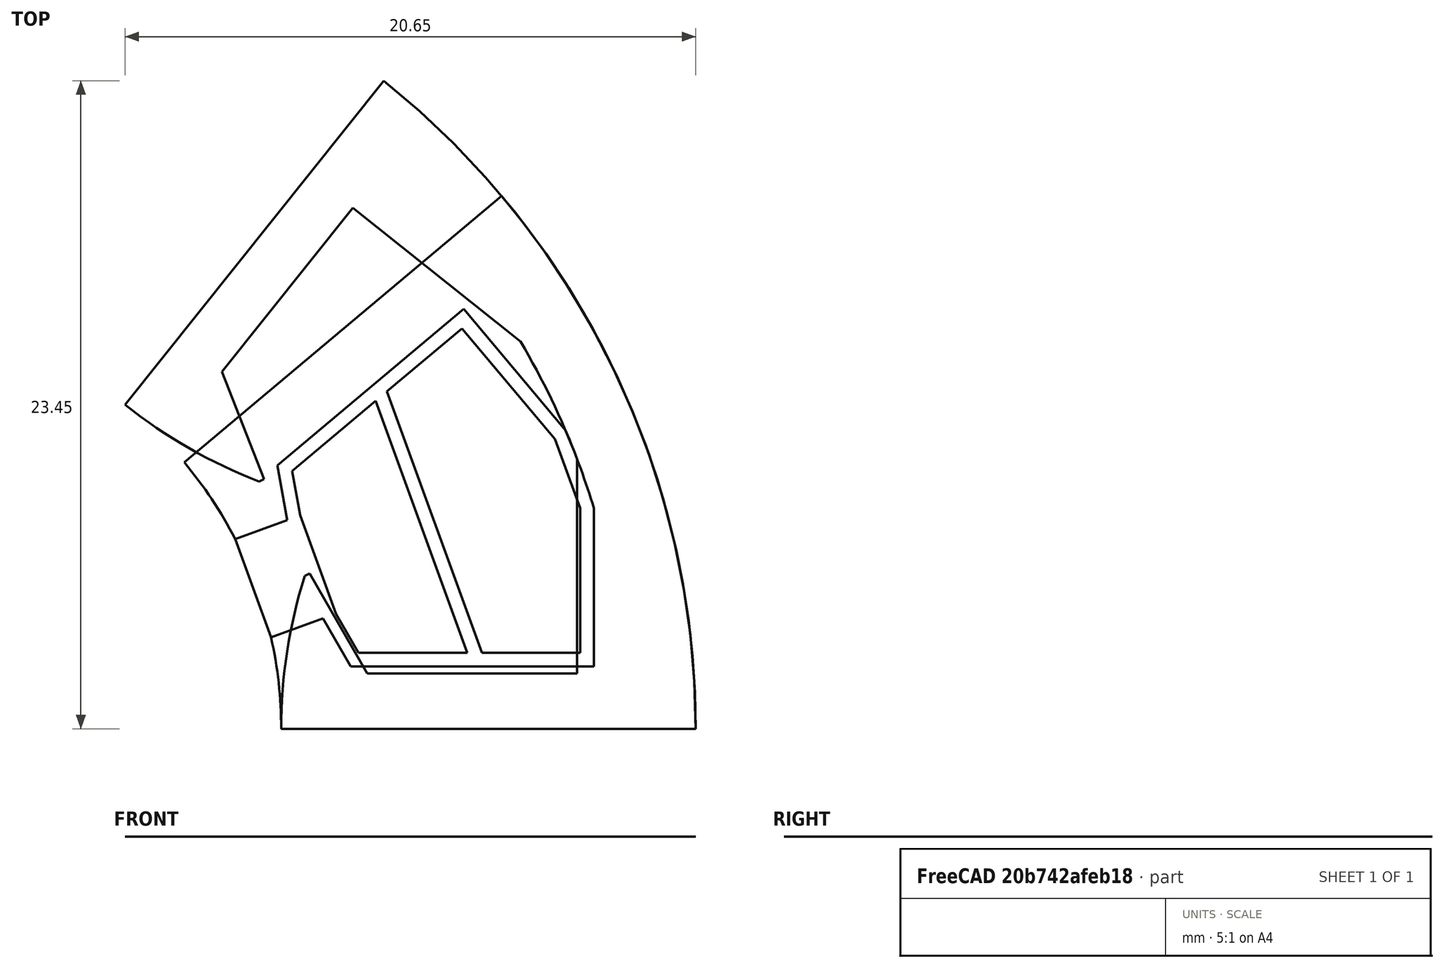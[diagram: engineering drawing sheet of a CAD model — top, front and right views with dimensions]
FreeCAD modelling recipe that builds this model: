
FCSTD DOCUMENT  (FreeCAD 0.18R4 (GitTag))
Label: StatorIRNeedleWindingCoilSpan
License: All rights reserved
LicenseURL: http://en.wikipedia.org/wiki/All_rights_reserved
objects: Sketcher::SketchObject×10, Surface::Filling×5, PartDesign::Body×2, Spreadsheet::Sheet×1
note: 17 computed .brp shape members not serialized (recipe doc carries the construction recipe); baked Part::Feature solids carry a one-line shape summary decoded from their .brp

FEATURE [Spreadsheet::Sheet] Spreadsheet  label="Variables"
  cells = A2=slotNumber; B2(slotNumber)=9; A3=outerDiameter; B3(outerDiameter)=60; A4=innerDiameter; B4(innerDiameter)=30; A5=stackLength; B5(stackLength)=20; A6=stackingFactor; B6(stackingFactor)=0.95; A7=cuttingThickness; B7(cuttingThickness)=0.1; A8=skewAngle; B8(skewAngle)=0; A9=segmentAngle; B9(segmentAngle)==360 / slotNumber; A10=tipHeightReduction; B10(tipHeightReduction)=0; A11=toothThickness; B11(toothThickness)=4.5; A12=yokeThickness; B12(yokeThickness)=2.5; A13=tipHeight; B13(tipHeight)=2; A14=tipAngle; B14(tipAngle)=120; A15=openingLeft; B15(openingLeft)=1.9; A16=openingRight; B16(openingRight)=1.9; A17=slotIsolation; B17(slotIsolation)=0.5; A18=windingAngle; B18(windingAngle)=35; A19=heightRatio; B19(heightRatio)=45; A20=roundingRadii; B20(roundingRadii)=0.2; A21=backWidth; B21(backWidth)=3; A22=backAngle; B22(backAngle)=90; A23=phaseSeparation; B23(phaseSeparation)=2; A24=axialOverhang; B24(axialOverhang)=1.2; A25=axialHeight; B25(axialHeight)=3
FEATURE [Sketcher::SketchObject] Sketch003  label="StatorSketch1"
  MapMode = 5
  Support = -> [XY_Plane]
  expr: Constraints[76] = Variables.backWidth
  expr: Constraints[37] = Variables.tipAngle
  expr: Constraints[60] = Variables.backAngle
  expr: Constraints[30] = Variables.tipHeight
  expr: Constraints[28] = Variables.openingRight
  expr: Constraints[32] = Variables.tipHeight * (1 - Variables.tipHeightReduction / 100)
  expr: Constraints[22] = Variables.openingLeft
  expr: Constraints[6] = Variables.outerDiameter / 2
  expr: Constraints[59] = Variables.tipHeight
  expr: Constraints[5] = Variables.segmentAngle
  expr: Constraints[11] = Variables.innerDiameter / 2
  expr: Constraints[54] = Variables.outerDiameter / 2 - Variables.yokeThickness
  expr: Constraints[49] = Variables.tipHeight * (1 - Variables.tipHeightReduction / 100)
  expr: Constraints[58] = Variables.toothThickness / 2
  expr: Constraints[18] = Variables.segmentAngle / 2
  expr: Constraints[50] = Variables.tipAngle
  expr: Constraints[52] = Variables.backAngle
  expr: Constraints[42] = Variables.toothThickness / 2
  sketch-geometry (27):
    g0: LineSegment [constr] StartX=0 StartY=0 StartZ=0 EndX=22.9813 EndY=19.2836 EndZ=0
    g1: LineSegment [constr] StartX=0 StartY=0 StartZ=0 EndX=30 EndY=0 EndZ=0
    g2: ArcOfCircle CenterX=0 CenterY=0 CenterZ=0 NormalX=0 NormalY=0 NormalZ=1 AngleXU=0 Radius=30 StartAngle=0 EndAngle=0.698132
    g3: ArcOfCircle [constr] CenterX=0 CenterY=0 CenterZ=0 NormalX=0 NormalY=0 NormalZ=1 AngleXU=0 Radius=15 StartAngle=0 EndAngle=0.698132
    g4: LineSegment [constr] StartX=13.3338 StartY=6.87098 StartZ=0 EndX=27.4859 EndY=12.0219 EndZ=0
    g5: LineSegment [constr] StartX=14.6308 StartY=3.30731 StartZ=0 EndX=28.7829 EndY=8.45826 EndZ=0
    g6: LineSegment [constr] StartX=28.1908 StartY=10.2606 StartZ=0 EndX=14.0954 EndY=5.1303 EndZ=0
    g7: LineSegment [constr] StartX=0 StartY=0 StartZ=0 EndX=14.0954 EndY=5.1303 EndZ=0
    g8: LineSegment [constr] StartX=13.3338 StartY=6.87098 StartZ=0 EndX=14.0954 EndY=5.1303 EndZ=0
    g9: LineSegment [constr] StartX=14.0954 StartY=5.1303 StartZ=0 EndX=14.6308 EndY=3.30731 EndZ=0
    g10: LineSegment [constr] StartX=13.3338 StartY=6.87098 StartZ=0 EndX=15.2132 EndY=7.55502 EndZ=0
    g11: LineSegment StartX=13.3338 StartY=6.87098 StartZ=0 EndX=15.2132 EndY=7.55502 EndZ=0
    g12: LineSegment StartX=15.2132 StartY=7.55502 StartZ=0 EndX=14.864 EndY=9.53521 EndZ=0
    g13: LineSegment StartX=14.864 StartY=9.53521 StartZ=0 EndX=21.6056 EndY=15.1921 EndZ=0
    g14: LineSegment [constr] StartX=14.864 StartY=9.53521 StartZ=0 EndX=13.4177 EndY=11.2588 EndZ=0
    g15: LineSegment StartX=21.6056 StartY=15.1921 StartZ=0 EndX=25.29 EndY=10.8011 EndZ=0
    g16: LineSegment StartX=26.3161 StartY=7.98201 StartZ=0 EndX=26.3161 EndY=2.25 EndZ=0
    g17: LineSegment StartX=26.3161 StartY=2.25 StartZ=0 EndX=17.5156 EndY=2.25 EndZ=0
    g18: LineSegment StartX=17.5156 StartY=2.25 StartZ=0 EndX=16.5102 EndY=3.99135 EndZ=0
    g19: LineSegment StartX=16.5102 StartY=3.99135 StartZ=0 EndX=14.6308 EndY=3.30731 EndZ=0
    g20: LineSegment [constr] StartX=26.3161 StartY=2.25 StartZ=0 EndX=26.3161 EndY=0 EndZ=0
    g21: LineSegment StartX=11.4907 StartY=9.64181 StartZ=0 EndX=22.9813 EndY=19.2836 EndZ=0
    g22: LineSegment StartX=30 StartY=0 StartZ=0 EndX=15 EndY=0 EndZ=0
    g23: ArcOfCircle CenterX=-3.78e-14 CenterY=0 CenterZ=0 NormalX=0 NormalY=0 NormalZ=1 AngleXU=0 Radius=15 StartAngle=0 EndAngle=0.222314
    g24: ArcOfCircle CenterX=-1.53e-14 CenterY=-1.29e-14 CenterZ=0 NormalX=0 NormalY=0 NormalZ=1 AngleXU=0 Radius=15 StartAngle=0.475817 EndAngle=0.698132
    g25: ArcOfCircle CenterX=0 CenterY=0 CenterZ=0 NormalX=0 NormalY=0 NormalZ=1 AngleXU=0 Radius=27.5 StartAngle=0.294493 EndAngle=0.403638
    g26: LineSegment [constr] StartX=25.29 StartY=10.8011 StartZ=0 EndX=26.3161 EndY=7.98201 EndZ=0
  constraints (77):
    c: Angle(g-1,g1) = 0
    c: Coincident(g0,g-1)
    c: Coincident(g1,g-1)
    c: Coincident(g2,g-1)
    c: Coincident(g2,g0)
    c: Angle(g1,g0) = 0.698132
    c: Radius(g2) = 30
    c: Coincident(g2,g1)
    c: Coincident(g3,g-1)
    c: PointOnObject(g3,g1)
    c: PointOnObject(g3,g0)
    c: Radius(g3) = 15
    c: PointOnObject(g4,g3)
    c: PointOnObject(g4,g2)
    c: PointOnObject(g5,g3)
    c: PointOnObject(g5,g2)
    c: PointOnObject(g6,g2)
    c: PointOnObject(g6,g3)
    c: Angle(g1,g6) = 0.349066
    c: Coincident(g7,g-1)
    c: Coincident(g7,g6)
    c: Coincident(g8,g4)
    c: Distance(g8) = 1.9
    c: Coincident(g8,g6)
    c: Parallel(g4,g6)
    c: Parallel(g5,g6)
    c: Coincident(g9,g6)
    c: Coincident(g9,g5)
    c: Distance(g9) = 1.9
    c: PointOnObject(g10,g4)
    c: Distance(g4,g10) = 2
    c: Angle(g4,g10) = 3.14159
    c: Distance(g10,g10) = 2
    c: Coincident(g11,g10)
    c: Coincident(g12,g11)
    c: Coincident(g13,g12)
    c: Coincident(g11,g10)
    c: Angle(g12,g13) = 2.0944
    c: Parallel(g0,g13)
    c: Coincident(g14,g12)
    c: PointOnObject(g14,g0)
    c: Angle(g13,g14) = 1.5708
    c: Distance(g14) = 2.25
    c: Coincident(g15,g13)
    c: Coincident(g17,g16)
    c: Coincident(g18,g17)
    c: PointOnObject(g18,g5)
    c: Coincident(g19,g18)
    c: PointOnObject(g19,g5)
    c: Distance(g19) = 2
    c: Angle(g17,g18) = 2.0944
    c: Parallel(g17,g1)
    c: Angle(g16,g17) = 1.5708
    c: Symmetric(g15,g16,g6)
    c: Distance(g-1,g15) = 27.5
    c: Coincident(g20,g16)
    c: PointOnObject(g20,g1)
    c: Vertical(g20)
    c: DistanceY(g20,g20) = 2.25
    c: Distance(g5,g18) = 2
    c: Angle(g13,g15) = 1.5708
    c: Coincident(g21,g3)
    c: Coincident(g21,g0)
    c: Coincident(g22,g2)
    c: Coincident(g22,g3)
    c: PointOnObject(g23,g-1)
    c: Coincident(g23,g19)
    c: Coincident(g23,g22)
    c: PointOnObject(g24,g0)
    c: Coincident(g24,g11)
    c: Coincident(g24,g21)
    c: Coincident(g25,g2)
    c: Coincident(g25,g15)
    c: Coincident(g25,g16)
    c: Coincident(g26,g15)
    c: Coincident(g26,g16)
    c: Distance(g26) = 3
FEATURE [Sketcher::SketchObject] Sketch  label="StatorStack"
  MapMode = 5
  Support = -> [XY_Plane001]
  expr: Constraints[20] = Variables.innerDiameter / 2
  expr: Constraints[10] = Variables.outerDiameter / 2
  expr: Constraints[9] = Variables.innerDiameter / 2
  expr: Constraints[8] = Variables.stackLength
  sketch-geometry (8):
    g0: LineSegment StartX=-10 StartY=15 StartZ=0 EndX=10 EndY=15 EndZ=0
    g1: LineSegment StartX=10 StartY=15 StartZ=0 EndX=10 EndY=30 EndZ=0
    g2: LineSegment StartX=10 StartY=30 StartZ=0 EndX=-10 EndY=30 EndZ=0
    g3: LineSegment StartX=-10 StartY=30 StartZ=0 EndX=-10 EndY=15 EndZ=0
    g4: LineSegment StartX=-10 StartY=-15 StartZ=0 EndX=10 EndY=-15 EndZ=0
    g5: LineSegment StartX=10 StartY=-15 StartZ=0 EndX=10 EndY=-30 EndZ=0
    g6: LineSegment StartX=10 StartY=-30 StartZ=0 EndX=-10 EndY=-30 EndZ=0
    g7: LineSegment StartX=-10 StartY=-30 StartZ=0 EndX=-10 EndY=-15 EndZ=0
  constraints (22):
    c: Coincident(g0,g1)
    c: Coincident(g1,g2)
    c: Coincident(g2,g3)
    c: Coincident(g3,g0)
    c: Horizontal(g2)
    c: Vertical(g1)
    c: Vertical(g3)
    c: Symmetric(g0,g0,g-2)
    c: DistanceX(g0,g0) = 20
    c: DistanceY(g-1,g0) = 15
    c: DistanceY(g-1,g1) = 30
    c: Coincident(g4,g5)
    c: Coincident(g5,g6)
    c: Coincident(g6,g7)
    c: Coincident(g7,g4)
    c: Horizontal(g6)
    c: Vertical(g5)
    c: Vertical(g7)
    c: Equal(g4,g0)
    c: Symmetric(g4,g4,g-2)
    c: DistanceY(g4,g-1) = 15
    c: Equal(g7,g3)
FEATURE [Sketcher::SketchObject] Sketch005  label="StatorSketch2"
  MapMode = 5
  Support = -> [XY_Plane]
  expr: Constraints[76] = Variables.backWidth
  expr: Constraints[28] = Variables.openingRight
  expr: Constraints[30] = Variables.tipHeight
  expr: Constraints[51] = Variables.tipAngle
  expr: Constraints[37] = Variables.tipAngle
  expr: Constraints[60] = Variables.tipHeight
  expr: Constraints[32] = Variables.tipHeight * (1 - Variables.tipHeightReduction / 100)
  expr: Constraints[61] = Variables.backAngle
  expr: Constraints[6] = Variables.outerDiameter / 2
  expr: Constraints[5] = Variables.segmentAngle
  expr: Constraints[22] = Variables.openingLeft
  expr: Constraints[55] = Variables.outerDiameter / 2 - Variables.yokeThickness
  expr: Constraints[59] = Variables.toothThickness / 2
  expr: Constraints[50] = Variables.tipHeight * (1 - Variables.tipHeightReduction / 100)
  expr: Constraints[18] = Variables.segmentAngle / 2
  expr: Constraints[11] = Variables.innerDiameter / 2
  expr: Constraints[53] = Variables.backAngle
  expr: Constraints[42] = Variables.toothThickness / 2
  sketch-geometry (27):
    g0: LineSegment [constr] StartX=0 StartY=0 StartZ=0 EndX=18.7047 EndY=23.4549 EndZ=0
    g1: LineSegment [constr] StartX=0 StartY=0 StartZ=0 EndX=30 EndY=0 EndZ=0
    g2: ArcOfCircle CenterX=0 CenterY=0 CenterZ=0 NormalX=0 NormalY=0 NormalZ=1 AngleXU=0 Radius=30 StartAngle=0 EndAngle=0.897598
    g3: ArcOfCircle [constr] CenterX=0 CenterY=0 CenterZ=0 NormalX=0 NormalY=0 NormalZ=1 AngleXU=0 Radius=15 StartAngle=0 EndAngle=0.897598
    g4: LineSegment [constr] StartX=12.5834 StartY=8.16445 StartZ=0 EndX=26.1523 EndY=14.6989 EndZ=0
    g5: LineSegment [constr] StartX=14.2288 StartY=4.74764 StartZ=0 EndX=27.7977 EndY=11.2821 EndZ=0
    g6: LineSegment [constr] StartX=27.0291 StartY=13.0165 StartZ=0 EndX=13.5145 EndY=6.50826 EndZ=0
    g7: LineSegment [constr] StartX=0 StartY=0 StartZ=0 EndX=13.5145 EndY=6.50826 EndZ=0
    g8: LineSegment [constr] StartX=12.5834 StartY=8.16445 StartZ=0 EndX=13.5145 EndY=6.50826 EndZ=0
    g9: LineSegment [constr] StartX=13.5145 StartY=6.50826 StartZ=0 EndX=14.2288 EndY=4.74764 EndZ=0
    g10: LineSegment [constr] StartX=14.2051 StartY=8.94544 StartZ=0 EndX=14.3853 EndY=9.03222 EndZ=0
    g11: LineSegment StartX=14.2051 StartY=8.94544 StartZ=0 EndX=14.3853 EndY=9.03222 EndZ=0
    g12: LineSegment StartX=14.3853 StartY=9.03222 StartZ=0 EndX=12.8601 EndY=12.9183 EndZ=0
    g13: LineSegment StartX=12.8601 StartY=12.9183 StartZ=0 EndX=17.5931 EndY=18.8533 EndZ=0
    g14: LineSegment [constr] StartX=12.8601 StartY=12.9183 StartZ=0 EndX=11.2965 EndY=14.1653 EndZ=0
    g15: LineSegment StartX=17.5931 StartY=18.8533 StartZ=0 EndX=23.6613 EndY=14.0141 EndZ=0
    g16: LineSegment [constr] StartX=23.6613 StartY=14.0141 StartZ=0 EndX=25.7092 EndY=9.7615 EndZ=0
    g17: LineSegment StartX=25.7092 StartY=9.7615 StartZ=0 EndX=25.7092 EndY=2 EndZ=0
    g18: LineSegment StartX=25.7092 StartY=2 StartZ=0 EndX=18.1181 EndY=2 EndZ=0
    g19: LineSegment StartX=18.1181 StartY=2 StartZ=0 EndX=16.0308 EndY=5.61541 EndZ=0
    g20: LineSegment StartX=16.0308 StartY=5.61541 StartZ=0 EndX=15.8506 EndY=5.52863 EndZ=0
    g21: LineSegment [constr] StartX=25.7092 StartY=2 StartZ=0 EndX=25.7092 EndY=0 EndZ=0
    g22: LineSegment StartX=9.35235 StartY=11.7275 StartZ=0 EndX=18.7047 EndY=23.4549 EndZ=0
    g23: LineSegment StartX=30 StartY=0 StartZ=0 EndX=15 EndY=0 EndZ=0
    g24: ArcOfCircle CenterX=20.8201 CenterY=26.1075 CenterZ=0 NormalX=0 NormalY=0 NormalZ=1 AngleXU=0 Radius=18.3928 StartAngle=4.03919 EndAngle=4.3445
    g25: ArcOfCircle CenterX=33.3928 CenterY=0 CenterZ=0 NormalX=0 NormalY=0 NormalZ=1 AngleXU=0 Radius=18.3928 StartAngle=2.83628 EndAngle=3.14159
    g26: ArcOfCircle CenterX=0 CenterY=0 CenterZ=0 NormalX=0 NormalY=0 NormalZ=1 AngleXU=0 Radius=27.5 StartAngle=0.362875 EndAngle=0.534723
  constraints (77):
    c: Angle(g-1,g1) = 0
    c: Coincident(g0,g-1)
    c: Coincident(g1,g-1)
    c: Coincident(g2,g-1)
    c: Coincident(g2,g0)
    c: Angle(g1,g0) = 0.698132
    c: Radius(g2) = 30
    c: Coincident(g2,g1)
    c: Coincident(g3,g-1)
    c: PointOnObject(g3,g1)
    c: PointOnObject(g3,g0)
    c: Radius(g3) = 15
    c: PointOnObject(g4,g3)
    c: PointOnObject(g4,g2)
    c: PointOnObject(g5,g3)
    c: PointOnObject(g5,g2)
    c: PointOnObject(g6,g2)
    c: PointOnObject(g6,g3)
    c: Angle(g1,g6) = 0.349066
    c: Coincident(g7,g-1)
    c: Coincident(g7,g6)
    c: Coincident(g8,g4)
    c: Distance(g8) = 1.9
    c: Coincident(g8,g6)
    c: Parallel(g4,g6)
    c: Parallel(g5,g6)
    c: Coincident(g9,g6)
    c: Coincident(g9,g5)
    c: Distance(g9) = 1.9
    c: PointOnObject(g10,g4)
    c: Distance(g4,g10) = 2
    c: Angle(g4,g10) = 3.14159
    c: Distance(g10,g10) = 2
    c: Coincident(g11,g10)
    c: Coincident(g12,g11)
    c: Coincident(g13,g12)
    c: Coincident(g11,g10)
    c: Angle(g12,g13) = 2.0944
    c: Parallel(g0,g13)
    c: Coincident(g14,g12)
    c: PointOnObject(g14,g0)
    c: Angle(g13,g14) = 1.5708
    c: Distance(g14) = 2.25
    c: Coincident(g15,g13)
    c: Coincident(g16,g15)
    c: Coincident(g17,g16)
    c: Coincident(g18,g17)
    c: Coincident(g19,g18)
    c: PointOnObject(g19,g5)
    c: Coincident(g20,g19)
    c: Distance(g20) = 2
    c: Angle(g18,g19) = 2.0944
    c: Parallel(g18,g1)
    c: Angle(g17,g18) = 1.5708
    c: Symmetric(g15,g16,g6)
    c: Distance(g-1,g15) = 27.5
    c: Coincident(g21,g17)
    c: PointOnObject(g21,g1)
    c: Vertical(g21)
    c: DistanceY(g21,g21) = 2.25
    c: Distance(g5,g19) = 2
    c: Angle(g13,g15) = 1.5708
    c: Coincident(g22,g3)
    c: Coincident(g22,g0)
    c: Coincident(g23,g2)
    c: Coincident(g23,g3)
    c: PointOnObject(g24,g22)
    c: Coincident(g24,g11)
    c: Coincident(g24,g22)
    c: Angle(g5,g20) = 3.14159
    c: PointOnObject(g25,g-1)
    c: Coincident(g25,g20)
    c: Coincident(g25,g23)
    c: Coincident(g26,g2)
    c: Coincident(g26,g15)
    c: Coincident(g26,g17)
    c: Distance(g16) = 3
FEATURE [Sketcher::SketchObject] Sketch008  label="SlotSketch"
  MapMode = 5
  Support = -> [XY_Plane]
  expr: Constraints[50] = Variables.toothThickness / 2
  expr: Constraints[18] = Variables.segmentAngle / 2
  expr: Constraints[30] = Variables.tipAngle
  expr: Constraints[51] = Variables.tipHeight
  expr: Constraints[28] = Variables.openingRight
  expr: Constraints[67] = Variables.backWidth
  expr: Constraints[46] = Variables.outerDiameter / 2 - Variables.yokeThickness
  expr: Constraints[22] = Variables.openingLeft
  expr: Constraints[6] = Variables.outerDiameter / 2
  expr: Constraints[44] = Variables.backAngle
  expr: Constraints[52] = Variables.backAngle
  expr: Constraints[11] = Variables.innerDiameter / 2
  expr: Constraints[5] = Variables.segmentAngle
  expr: Constraints[42] = Variables.tipAngle
  expr: Constraints[35] = Variables.toothThickness / 2
  sketch-geometry (25):
    g0: LineSegment [constr] StartX=0 StartY=0 StartZ=0 EndX=22.9813 EndY=19.2836 EndZ=0
    g1: LineSegment [constr] StartX=0 StartY=0 StartZ=0 EndX=30 EndY=0 EndZ=0
    g2: ArcOfCircle [constr] CenterX=0 CenterY=0 CenterZ=0 NormalX=0 NormalY=0 NormalZ=1 AngleXU=0 Radius=30 StartAngle=0 EndAngle=0.698132
    g3: ArcOfCircle [constr] CenterX=0 CenterY=0 CenterZ=0 NormalX=0 NormalY=0 NormalZ=1 AngleXU=0 Radius=15 StartAngle=0 EndAngle=0.698132
    g4: LineSegment [constr] StartX=13.3338 StartY=6.87098 StartZ=0 EndX=27.4859 EndY=12.0219 EndZ=0
    g5: LineSegment [constr] StartX=14.6308 StartY=3.30731 StartZ=0 EndX=28.7829 EndY=8.45826 EndZ=0
    g6: LineSegment [constr] StartX=28.1908 StartY=10.2606 StartZ=0 EndX=14.0954 EndY=5.1303 EndZ=0
    g7: LineSegment [constr] StartX=0 StartY=0 StartZ=0 EndX=14.0954 EndY=5.1303 EndZ=0
    g8: LineSegment [constr] StartX=13.3338 StartY=6.87098 StartZ=0 EndX=14.0954 EndY=5.1303 EndZ=0
    g9: LineSegment [constr] StartX=14.0954 StartY=5.1303 StartZ=0 EndX=14.6308 EndY=3.30731 EndZ=0
    g10: LineSegment StartX=15.2132 StartY=7.55502 StartZ=0 EndX=14.864 EndY=9.53521 EndZ=0
    g11: LineSegment StartX=14.864 StartY=9.53521 StartZ=0 EndX=21.6056 EndY=15.1921 EndZ=0
    g12: LineSegment [constr] StartX=14.864 StartY=9.53521 StartZ=0 EndX=13.4177 EndY=11.2588 EndZ=0
    g13: LineSegment StartX=21.6056 StartY=15.1921 StartZ=0 EndX=25.29 EndY=10.8011 EndZ=0
    g14: LineSegment [constr] StartX=25.29 StartY=10.8011 StartZ=0 EndX=26.3161 EndY=7.98201 EndZ=0
    g15: LineSegment StartX=26.3161 StartY=7.98201 StartZ=0 EndX=26.3161 EndY=2.25 EndZ=0
    g16: LineSegment StartX=26.3161 StartY=2.25 StartZ=0 EndX=17.5156 EndY=2.25 EndZ=0
    g17: LineSegment StartX=17.5156 StartY=2.25 StartZ=0 EndX=16.5102 EndY=3.99135 EndZ=0
    g18: LineSegment [constr] StartX=26.3161 StartY=2.25 StartZ=0 EndX=26.3161 EndY=0 EndZ=0
    g19: LineSegment [constr] StartX=11.4907 StartY=9.64181 StartZ=0 EndX=22.9813 EndY=19.2836 EndZ=0
    g20: LineSegment [constr] StartX=30 StartY=0 StartZ=0 EndX=15 EndY=0 EndZ=0
    g21: LineSegment StartX=13.3338 StartY=6.87098 StartZ=0 EndX=14.6308 EndY=3.30731 EndZ=0
    g22: LineSegment StartX=13.3338 StartY=6.87098 StartZ=0 EndX=15.2132 EndY=7.55502 EndZ=0
    g23: LineSegment StartX=14.6308 StartY=3.30731 StartZ=0 EndX=16.5102 EndY=3.99135 EndZ=0
    g24: ArcOfCircle CenterX=0 CenterY=0 CenterZ=0 NormalX=0 NormalY=0 NormalZ=1 AngleXU=0 Radius=27.5 StartAngle=0.294493 EndAngle=0.403638
  constraints (68):
    c: Angle(g-1,g1) = 0
    c: Coincident(g0,g-1)
    c: Coincident(g1,g-1)
    c: Coincident(g2,g-1)
    c: Coincident(g2,g0)
    c: Angle(g1,g0) = 0.698132
    c: Radius(g2) = 30
    c: Coincident(g2,g1)
    c: Coincident(g3,g-1)
    c: PointOnObject(g3,g1)
    c: PointOnObject(g3,g0)
    c: Radius(g3) = 15
    c: PointOnObject(g4,g3)
    c: PointOnObject(g4,g2)
    c: PointOnObject(g5,g3)
    c: PointOnObject(g5,g2)
    c: PointOnObject(g6,g2)
    c: PointOnObject(g6,g3)
    c: Angle(g1,g6) = 0.349066
    c: Coincident(g7,g-1)
    c: Coincident(g7,g6)
    c: Coincident(g8,g4)
    c: Distance(g8) = 1.9
    c: Coincident(g8,g6)
    c: Parallel(g4,g6)
    c: Parallel(g5,g6)
    c: Coincident(g9,g6)
    c: Coincident(g9,g5)
    c: Distance(g9) = 1.9
    c: Coincident(g11,g10)
    c: Angle(g10,g11) = 2.0944
    c: Parallel(g0,g11)
    c: Coincident(g12,g10)
    c: PointOnObject(g12,g0)
    c: Angle(g11,g12) = 1.5708
    c: Distance(g12) = 2.25
    c: Coincident(g13,g11)
    c: Coincident(g14,g13)
    c: Coincident(g15,g14)
    c: Coincident(g16,g15)
    c: Coincident(g17,g16)
    c: PointOnObject(g17,g5)
    c: Angle(g16,g17) = 2.0944
    c: Parallel(g16,g1)
    c: Angle(g15,g16) = 1.5708
    c: Symmetric(g13,g14,g6)
    c: Distance(g-1,g13) = 27.5
    c: Coincident(g18,g15)
    c: PointOnObject(g18,g1)
    c: Vertical(g18)
    c: DistanceY(g18,g18) = 2.25
    c: Distance(g5,g17) = 2
    c: Angle(g11,g13) = 1.5708
    c: Coincident(g19,g3)
    c: Coincident(g19,g0)
    c: Coincident(g20,g2)
    c: Coincident(g20,g3)
    c: Symmetric(g17,g10,g6)
    c: Coincident(g21,g4)
    c: Coincident(g21,g5)
    c: Coincident(g22,g21)
    c: Coincident(g22,g10)
    c: Coincident(g23,g21)
    c: Coincident(g23,g17)
    c: Coincident(g24,g-1)
    c: Coincident(g24,g13)
    c: Coincident(g24,g15)
    c: Distance(g14) = 3
FEATURE [Surface::Filling] Surface  label="SlotSketch_Surface"
  Anisotropy = false
  BoundaryEdges = -> [Sketch008]
  BoundaryOrder = [0,0,0,0,0,0,0,0,0,0]
  Degree = 3
  Iterations = 2
  MaximumDegree = 8
  MaximumSegments = 9
  PointsOnCurve = 15
  TolAngular = 0.01
  TolCurvature = 0.1
  Tolerance2d = 1e-05
  Tolerance3d = 0.0001
FEATURE [Surface::Filling] Surface001  label="StatorSketch2_Surface"
  Anisotropy = false
  BoundaryEdges = -> [Sketch005]
  BoundaryOrder = [0,0,0,0,0,0,0,0,0,0,0,0,0,0]
  Degree = 3
  Iterations = 2
  MaximumDegree = 8
  MaximumSegments = 9
  PointsOnCurve = 15
  TolAngular = 0.01
  TolCurvature = 0.1
  Tolerance2d = 1e-05
  Tolerance3d = 0.0001
FEATURE [Surface::Filling] Surface002  label="StatorSketch1_Surface"
  Anisotropy = false
  BoundaryEdges = -> [Sketch003]
  BoundaryOrder = [0,0,0,0,0,0,0,0,0,0,0,0,0,0]
  Degree = 3
  Iterations = 2
  MaximumDegree = 8
  MaximumSegments = 9
  PointsOnCurve = 15
  TolAngular = 0.01
  TolCurvature = 0.1
  Tolerance2d = 1e-05
  Tolerance3d = 0.0001
FEATURE [Sketcher::SketchObject] Sketch010  label="ToothLine"
  ExternalGeometry = -> [Sketch008]
  MapMode = 5
  Support = -> [XY_Plane]
  expr: Constraints[0] = Variables.toothThickness
  sketch-geometry (1):
    g0: LineSegment StartX=18.2348 StartY=12.3636 StartZ=0 EndX=15.3422 EndY=15.8108 EndZ=0
  constraints (3):
    c: Distance(g0) = 4.5
    c: Symmetric(g-3,g-3,g0)
    c: Angle(g-3,g0) = 1.5708
FEATURE [Sketcher::SketchObject] Sketch006  label="TerminalLeftSketch"
  ExternalGeometry = -> [Sketch008,Sketch010]
  MapMode = 5
  Support = -> [XY_Plane]
  expr: Constraints[11] = Variables.slotIsolation
  sketch-geometry (18):
    g0: LineSegment [constr] StartX=0 StartY=0 StartZ=0 EndX=15.8617 EndY=5.77319 EndZ=0
    g1: LineSegment [constr] StartX=18.2348 StartY=12.3636 StartZ=0 EndX=21.9159 EndY=2.25 EndZ=0
    g2: LineSegment [constr] StartX=18.6424 StartY=12.7057 StartZ=0 EndX=22.4479 EndY=2.25 EndZ=0
    g3: LineSegment [constr] StartX=18.2348 StartY=12.3636 StartZ=0 EndX=18.7046 EndY=12.5347 EndZ=0
    g4: LineSegment [constr] StartX=18.4168 StartY=11.8636 StartZ=0 EndX=15.3998 EndY=9.33211 EndZ=0
    g5: LineSegment [constr] StartX=15.3998 StartY=9.33211 StartZ=0 EndX=15.683 EndY=7.72603 EndZ=0
    g6: LineSegment [constr] StartX=15.683 StartY=7.72603 StartZ=0 EndX=16.9801 EndY=4.16236 EndZ=0
    g7: LineSegment [constr] StartX=16.9801 StartY=4.16236 StartZ=0 EndX=17.7955 EndY=2.75 EndZ=0
    g8: LineSegment [constr] StartX=17.7955 StartY=2.75 StartZ=0 EndX=21.7339 EndY=2.75 EndZ=0
    g9: LineSegment [constr] StartX=15.683 StartY=7.72603 StartZ=0 EndX=15.2132 EndY=7.55502 EndZ=0
    g10: LineSegment [constr] StartX=15.3998 StartY=9.33211 StartZ=0 EndX=15.0784 EndY=9.71513 EndZ=0
    g11: LineSegment [constr] StartX=17.7955 StartY=2.75 StartZ=0 EndX=17.7955 EndY=2.25 EndZ=0
    g12: LineSegment StartX=15.683 StartY=7.72603 StartZ=0 EndX=15.3998 EndY=9.33211 EndZ=0
    g13: LineSegment StartX=15.3998 StartY=9.33211 StartZ=0 EndX=18.4168 EndY=11.8636 EndZ=0
    g14: LineSegment StartX=18.4168 StartY=11.8636 StartZ=0 EndX=21.7339 EndY=2.75 EndZ=0
    g15: LineSegment StartX=21.7339 StartY=2.75 StartZ=0 EndX=17.7955 EndY=2.75 EndZ=0
    g16: LineSegment StartX=17.7955 StartY=2.75 StartZ=0 EndX=16.9801 EndY=4.16236 EndZ=0
    g17: LineSegment StartX=16.9801 StartY=4.16236 StartZ=0 EndX=15.683 EndY=7.72603 EndZ=0
  constraints (48):
    c: Symmetric(g-5,g-6,g0)
    c: Coincident(g0,g-1)
    c: Coincident(g1,g-10)
    c: PointOnObject(g1,g-7)
    c: Angle(g0,g1) = 1.5708
    c: PointOnObject(g2,g-4)
    c: PointOnObject(g2,g-7)
    c: Parallel(g2,g1)
    c: Coincident(g3,g1)
    c: PointOnObject(g3,g2)
    c: Angle(g1,g3) = 1.5708
    c: Distance(g3) = 0.5
    c: PointOnObject(g4,g1)
    c: Coincident(g5,g4)
    c: Coincident(g6,g5)
    c: Coincident(g7,g6)
    c: Coincident(g8,g7)
    c: PointOnObject(g8,g1)
    c: Parallel(g-4,g4)
    c: Parallel(g8,g-7)
    c: Parallel(g-5,g5)
    c: Parallel(g7,g-6)
    c: Symmetric(g5,g6,g0)
    c: Coincident(g9,g5)
    c: Coincident(g9,g-5)
    c: Angle(g9,g6) = 1.5708
    c: Angle(g9,g6) = 1.5708
    c: Equal(g3,g9)
    c: Coincident(g10,g4)
    c: PointOnObject(g10,g-4)
    c: Angle(g4,g10) = 1.5708
    c: Equal(g10,g9)
    c: Coincident(g11,g7)
    c: PointOnObject(g11,g-7)
    c: Angle(g11,g8) = 1.5708
    c: Equal(g9,g11)
    c: Coincident(g12,g5)
    c: Coincident(g12,g4)
    c: Coincident(g13,g12)
    c: Coincident(g13,g4)
    c: Coincident(g14,g13)
    c: Coincident(g14,g8)
    c: Coincident(g15,g14)
    c: Coincident(g15,g7)
    c: Coincident(g16,g15)
    c: Coincident(g16,g6)
    c: Coincident(g17,g16)
    c: Coincident(g17,g12)
FEATURE [Sketcher::SketchObject] Sketch007  label="TerminalRightSketch"
  ExternalGeometry = -> [Sketch008,Sketch006]
  MapMode = 5
  Support = -> [XY_Plane]
  expr: Constraints[17] = Variables.slotIsolation
  sketch-geometry (11):
    g0: LineSegment [constr] StartX=0 StartY=0 StartZ=0 EndX=15.8617 EndY=5.77319 EndZ=0
    g1: LineSegment StartX=18.8244 StartY=12.2057 StartZ=0 EndX=21.544 EndY=14.4877 EndZ=0
    g2: LineSegment StartX=21.544 StartY=14.4877 StartZ=0 EndX=24.907 EndY=10.4797 EndZ=0
    g3: LineSegment StartX=24.907 StartY=10.4797 StartZ=0 EndX=25.8161 EndY=7.98201 EndZ=0
    g4: LineSegment StartX=25.8161 StartY=7.98201 StartZ=0 EndX=25.8161 EndY=2.75 EndZ=0
    g5: LineSegment StartX=25.8161 StartY=2.75 StartZ=0 EndX=22.266 EndY=2.75 EndZ=0
    g6: LineSegment StartX=22.266 StartY=2.75 StartZ=0 EndX=18.8244 EndY=12.2057 EndZ=0
    g7: LineSegment [constr] StartX=24.907 StartY=10.4797 StartZ=0 EndX=25.29 EndY=10.8011 EndZ=0
    g8: LineSegment [constr] StartX=18.4168 StartY=11.8636 StartZ=0 EndX=18.8866 EndY=12.0347 EndZ=0
    g9: LineSegment [constr] StartX=18.8244 StartY=12.2057 StartZ=0 EndX=18.503 EndY=12.5887 EndZ=0
    g10: LineSegment [constr] StartX=25.8161 StartY=7.98201 StartZ=0 EndX=26.3161 EndY=7.98201 EndZ=0
  constraints (29):
    c: Symmetric(g-5,g-6,g0)
    c: Coincident(g0,g-1)
    c: Coincident(g2,g1)
    c: Coincident(g3,g2)
    c: Coincident(g4,g3)
    c: Coincident(g5,g4)
    c: Horizontal(g5)
    c: Coincident(g6,g5)
    c: Coincident(g6,g1)
    c: Parallel(g6,g-10)
    c: Parallel(g2,g-3)
    c: Symmetric(g2,g3,g0)
    c: Parallel(g1,g-4)
    c: Symmetric(g4,g1,g0)
    c: Coincident(g7,g2)
    c: PointOnObject(g7,g-3)
    c: Angle(g7,g2) = 1.5708
    c: Distance(g7) = 0.5
    c: Coincident(g8,g-10)
    c: PointOnObject(g8,g6)
    c: Angle(g-10,g8) = 1.5708
    c: Equal(g8,g7)
    c: Coincident(g9,g1)
    c: PointOnObject(g9,g-4)
    c: Angle(g1,g9) = 1.5708
    c: Equal(g9,g8)
    c: Coincident(g10,g3)
    c: Coincident(g10,g-9)
    c: Angle(g4,g10) = 1.5708
FEATURE [Surface::Filling] Surface003  label="TerminalRightSketch_Surface"
  Anisotropy = false
  BoundaryEdges = -> [Sketch007]
  BoundaryOrder = [0,0,0,0,0,0]
  Degree = 3
  Iterations = 2
  MaximumDegree = 8
  MaximumSegments = 9
  PointsOnCurve = 15
  TolAngular = 0.01
  TolCurvature = 0.1
  Tolerance2d = 1e-05
  Tolerance3d = 0.0001
FEATURE [Surface::Filling] Surface004  label="TerminalLeftSketch_Surface"
  Anisotropy = false
  BoundaryEdges = -> [Sketch006]
  BoundaryOrder = [0,0,0,0,0,0]
  Degree = 3
  Iterations = 2
  MaximumDegree = 8
  MaximumSegments = 9
  PointsOnCurve = 15
  TolAngular = 0.01
  TolCurvature = 0.1
  Tolerance2d = 1e-05
  Tolerance3d = 0.0001
FEATURE [Sketcher::SketchObject] Sketch011  label="YokeLine"
  ExternalGeometry = -> [Sketch008]
  MapMode = 5
  Support = -> [XY_Plane]
  expr: Constraints[7] = Variables.outerDiameter / 2
  sketch-geometry (3):
    g0: LineSegment [constr] StartX=25.29 StartY=10.8011 StartZ=0 EndX=26.3161 EndY=7.98201 EndZ=0
    g1: LineSegment StartX=25.8415 StartY=9.40555 StartZ=0 EndX=28.1908 EndY=10.2606 EndZ=0
    g2: LineSegment [constr] StartX=25.8415 StartY=9.40555 StartZ=0 EndX=25.8031 EndY=9.39155 EndZ=0
  constraints (8):
    c: Coincident(g2,g1)
    c: Angle(g0,g2) = 1.5708
    c: Symmetric(g0,g0,g2)
    c: Parallel(g2,g1)
    c: Coincident(g0,g-3)
    c: Coincident(g0,g-3)
    c: PointOnObject(g1,g-3)
    c: Distance(g-1,g1) = 30
FEATURE [Sketcher::SketchObject] Sketch012  label="Isolation"
  ExternalGeometry = -> [Sketch]
  MapMode = 5
  Support = -> [XY_Plane001]
  expr: Constraints[75] = Variables.axialHeight / 2
  expr: Constraints[9] = Variables.axialHeight + Variables.axialOverhang
  expr: Constraints[10] = Variables.axialHeight
  expr: Constraints[13] = (Variables.outerDiameter - Variables.innerDiameter) / 2 - Variables.yokeThickness - Variables.tipHeight
  expr: Constraints[12] = Variables.yokeThickness
  expr: Constraints[11] = Variables.tipHeight
  sketch-geometry (32):
    g0: LineSegment StartX=-10 StartY=30 StartZ=0 EndX=-10 EndY=15 EndZ=0
    g1: LineSegment StartX=-10 StartY=15 StartZ=0 EndX=-12.7 EndY=15 EndZ=0
    g2: LineSegment StartX=-12.7 StartY=15 StartZ=0 EndX=-12.7 EndY=17 EndZ=0
    g3: LineSegment StartX=-12.7 StartY=17 StartZ=0 EndX=-11.2 EndY=17 EndZ=0
    g4: LineSegment StartX=-11.2 StartY=17 StartZ=0 EndX=-11.2 EndY=27.5 EndZ=0
    g5: LineSegment StartX=-11.2 StartY=27.5 StartZ=0 EndX=-14.2 EndY=27.5 EndZ=0
    g6: LineSegment StartX=-14.2 StartY=27.5 StartZ=0 EndX=-14.2 EndY=30 EndZ=0
    g7: LineSegment StartX=-14.2 StartY=30 StartZ=0 EndX=-10 EndY=30 EndZ=0
    g8: LineSegment StartX=-12.7 StartY=-15 StartZ=0 EndX=-10 EndY=-15 EndZ=0
    g9: LineSegment StartX=-10 StartY=-15 StartZ=0 EndX=-10 EndY=-30 EndZ=0
    g10: LineSegment StartX=-10 StartY=-30 StartZ=0 EndX=-14.2 EndY=-30 EndZ=0
    g11: LineSegment StartX=-14.2 StartY=-30 StartZ=0 EndX=-14.2 EndY=-27.5 EndZ=0
    g12: LineSegment StartX=-14.2 StartY=-27.5 StartZ=0 EndX=-11.2 EndY=-27.5 EndZ=0
    g13: LineSegment StartX=-11.2 StartY=-27.5 StartZ=0 EndX=-11.2 EndY=-17 EndZ=0
    g14: LineSegment StartX=-11.2 StartY=-17 StartZ=0 EndX=-12.7 EndY=-17 EndZ=0
    g15: LineSegment StartX=-12.7 StartY=-17 StartZ=0 EndX=-12.7 EndY=-15 EndZ=0
    g16: LineSegment StartX=14.2 StartY=30 StartZ=0 EndX=10 EndY=30 EndZ=0
    g17: LineSegment StartX=10 StartY=30 StartZ=0 EndX=10 EndY=15 EndZ=0
    g18: LineSegment StartX=10 StartY=15 StartZ=0 EndX=12.7 EndY=15 EndZ=0
    g19: LineSegment StartX=12.7 StartY=15 StartZ=0 EndX=12.7 EndY=17 EndZ=0
    g20: LineSegment StartX=12.7 StartY=17 StartZ=0 EndX=11.2 EndY=17 EndZ=0
    g21: LineSegment StartX=11.2 StartY=17 StartZ=0 EndX=11.2 EndY=27.5 EndZ=0
    g22: LineSegment StartX=11.2 StartY=27.5 StartZ=0 EndX=14.2 EndY=27.5 EndZ=0
    g23: LineSegment StartX=14.2 StartY=27.5 StartZ=0 EndX=14.2 EndY=30 EndZ=0
    g24: LineSegment StartX=12.7 StartY=-15 StartZ=0 EndX=10 EndY=-15 EndZ=0
    g25: LineSegment StartX=10 StartY=-15 StartZ=0 EndX=10 EndY=-30 EndZ=0
    g26: LineSegment StartX=10 StartY=-30 StartZ=0 EndX=14.2 EndY=-30 EndZ=0
    g27: LineSegment StartX=14.2 StartY=-30 StartZ=0 EndX=14.2 EndY=-27.5 EndZ=0
    g28: LineSegment StartX=14.2 StartY=-27.5 StartZ=0 EndX=11.2 EndY=-27.5 EndZ=0
    g29: LineSegment StartX=11.2 StartY=-27.5 StartZ=0 EndX=11.2 EndY=-17 EndZ=0
    g30: LineSegment StartX=11.2 StartY=-17 StartZ=0 EndX=12.7 EndY=-17 EndZ=0
    g31: LineSegment StartX=12.7 StartY=-17 StartZ=0 EndX=12.7 EndY=-15 EndZ=0
  constraints (91):
    c: Coincident(g1,g0)
    c: Coincident(g2,g1)
    c: Coincident(g3,g2)
    c: Coincident(g4,g3)
    c: Vertical(g4)
    c: Coincident(g5,g4)
    c: Coincident(g7,g6)
    c: Coincident(g7,g0)
    c: Coincident(g6,g5)
    c: DistanceX(g7,g7) = 4.2
    c: DistanceX(g5,g5) = 3
    c: DistanceY(g2,g2) = 2
    c: DistanceY(g6,g6) = 2.5
    c: DistanceY(g4,g4) = 10.5
    c: Coincident(g0,g-6)
    c: Coincident(g8,g9)
    c: Vertical(g9)
    c: Coincident(g9,g10)
    c: Coincident(g10,g11)
    c: Coincident(g11,g12)
    c: Coincident(g12,g13)
    c: Vertical(g13)
    c: Coincident(g13,g14)
    c: Coincident(g14,g15)
    c: Coincident(g15,g8)
    c: Equal(g7,g10)
    c: Vertical(g11)
    c: Equal(g13,g4)
    c: Equal(g9,g0)
    c: Equal(g11,g6)
    c: Coincident(g8,g-4)
    c: Coincident(g16,g17)
    c: Vertical(g17)
    c: Coincident(g17,g18)
    c: Coincident(g18,g19)
    c: Coincident(g19,g20)
    c: Coincident(g20,g21)
    c: Vertical(g21)
    c: Coincident(g21,g22)
    c: Coincident(g22,g23)
    c: Coincident(g23,g16)
    c: Equal(g0,g17)
    c: Equal(g16,g7)
    c: Equal(g2,g19)
    c: Equal(g6,g23)
    c: Coincident(g-3,g16)
    c: Coincident(g24,g25)
    c: Vertical(g25)
    c: Coincident(g25,g26)
    c: Coincident(g26,g27)
    c: Vertical(g27)
    c: Coincident(g27,g28)
    c: Coincident(g28,g29)
    c: Vertical(g29)
    c: Coincident(g29,g30)
    c: Coincident(g30,g31)
    c: Coincident(g31,g24)
    c: Equal(g8,g24)
    c: Equal(g10,g26)
    c: Equal(g11,g27)
    c: Equal(g15,g31)
    c: Equal(g9,g25)
    c: Coincident(g24,g-5)
    c: Angle(g17,g16) = 1.5708
    c: Angle(g21,g22) = 1.5708
    c: Angle(g18,g17) = 1.5708
    c: Angle(g20,g21) = 1.5708
    c: Angle(g25,g24) = 1.5708
    c: Angle(g29,g30) = 1.5708
    c: Angle(g28,g29) = 1.5708
    c: Angle(g26,g25) = 1.5708
    c: Angle(g14,g13) = 1.5708
    c: Angle(g13,g12) = 1.5708
    c: Angle(g9,g10) = 1.5708
    c: Angle(g8,g9) = 1.5708
    c: DistanceX(g3,g3) = 1.5
    c: Angle(g6,g7) = 1.5708
    c: Equal(g20,g3)
    c: Equal(g3,g14)
    c: Angle(g15,g8) = 1.5708
    c: Equal(g12,g5)
    c: Equal(g28,g5)
    c: Equal(g5,g22)
    c: Angle(g24,g31) = 1.5708
    c: Angle(g19,g18) = 1.5708
    c: Angle(g23,g22) = 1.5708
    c: Angle(g5,g4) = 1.5708
    c: Coincident(g0,g-6)
    c: Angle(g1,g2) = 1.5708
    c: Angle(g7,g0) = 1.5708
    c: Angle(g0,g1) = 1.5708
FEATURE [PartDesign::Body] Body001  label="SideView"
  Group = -> [Sketch,Sketch012]
  Origin = -> Origin001
FEATURE [Sketcher::SketchObject] Sketch013  label="TerminalSingleSketch"
  ExternalGeometry = -> [Sketch008]
  MapMode = 5
  Support = -> [XY_Plane]
  expr: Constraints[44] = Variables.backWidth
  expr: Constraints[37] = Variables.slotIsolation
  sketch-geometry (21):
    g0: LineSegment [constr] StartX=0 StartY=0 StartZ=0 EndX=15.8617 EndY=5.77319 EndZ=0
    g1: LineSegment [constr] StartX=15.4065 StartY=9.33775 StartZ=0 EndX=21.544 EndY=14.4877 EndZ=0
    g2: LineSegment [constr] StartX=21.544 StartY=14.4877 StartZ=0 EndX=24.79 EndY=10.6191 EndZ=0
    g3: LineSegment [constr] StartX=24.79 StartY=10.6191 StartZ=0 EndX=25.8161 EndY=7.80003 EndZ=0
    g4: LineSegment [constr] StartX=25.8161 StartY=7.80003 StartZ=0 EndX=25.8161 EndY=2.75 EndZ=0
    g5: LineSegment [constr] StartX=25.8161 StartY=2.75 StartZ=0 EndX=17.8043 EndY=2.75 EndZ=0
    g6: LineSegment [constr] StartX=15.4065 StartY=9.33775 StartZ=0 EndX=15.7056 EndY=7.64184 EndZ=0
    g7: LineSegment [constr] StartX=15.7056 StartY=7.64184 StartZ=0 EndX=16.9432 EndY=4.24135 EndZ=0
    g8: LineSegment [constr] StartX=16.9432 StartY=4.24135 StartZ=0 EndX=17.8043 EndY=2.75 EndZ=0
    g9: LineSegment StartX=15.4065 StartY=9.33775 StartZ=0 EndX=21.544 EndY=14.4877 EndZ=0
    g10: LineSegment StartX=21.544 StartY=14.4877 StartZ=0 EndX=24.79 EndY=10.6191 EndZ=0
    g11: LineSegment StartX=24.79 StartY=10.6191 StartZ=0 EndX=25.8161 EndY=7.80003 EndZ=0
    g12: LineSegment StartX=25.8161 StartY=7.80003 StartZ=0 EndX=25.8161 EndY=2.75 EndZ=0
    g13: LineSegment StartX=25.8161 StartY=2.75 StartZ=0 EndX=17.8043 EndY=2.75 EndZ=0
    g14: LineSegment StartX=17.8043 StartY=2.75 StartZ=0 EndX=16.9432 EndY=4.24135 EndZ=0
    g15: LineSegment StartX=16.9432 StartY=4.24135 StartZ=0 EndX=15.7056 EndY=7.64184 EndZ=0
    g16: LineSegment StartX=15.7056 StartY=7.64184 StartZ=0 EndX=15.4065 EndY=9.33775 EndZ=0
    g17: LineSegment [constr] StartX=15.4065 StartY=9.33775 StartZ=0 EndX=15.0851 EndY=9.72077 EndZ=0
    g18: LineSegment [constr] StartX=15.4065 StartY=9.33775 StartZ=0 EndX=14.9141 EndY=9.25092 EndZ=0
    g19: LineSegment [constr] StartX=15.7056 StartY=7.64184 StartZ=0 EndX=15.2132 EndY=7.55502 EndZ=0
    g20: LineSegment [constr] StartX=24.79 StartY=10.6191 StartZ=0 EndX=25.1731 EndY=10.9405 EndZ=0
  constraints (50):
    c: Symmetric(g-5,g-6,g0)
    c: Coincident(g0,g-1)
    c: Coincident(g2,g1)
    c: Coincident(g3,g2)
    c: Coincident(g4,g3)
    c: Coincident(g5,g4)
    c: Coincident(g6,g1)
    c: Coincident(g7,g6)
    c: Coincident(g8,g7)
    c: Coincident(g8,g5)
    c: Coincident(g9,g1)
    c: Coincident(g9,g1)
    c: Coincident(g10,g9)
    c: Coincident(g10,g2)
    c: Coincident(g11,g10)
    c: Coincident(g11,g3)
    c: Coincident(g12,g11)
    c: Coincident(g12,g4)
    c: Coincident(g13,g12)
    c: Coincident(g13,g5)
    c: Coincident(g14,g13)
    c: Coincident(g14,g7)
    c: Coincident(g15,g14)
    c: Coincident(g15,g6)
    c: Coincident(g16,g15)
    c: Coincident(g16,g9)
    c: Angle(g-4) = 0.698132
    c: Coincident(g17,g9)
    c: Coincident(g18,g9)
    c: PointOnObject(g18,g-5)
    c: Angle(g18,g16) = 1.5708
    c: Angle(g9,g17) = 1.5708
    c: Equal(g17,g18)
    c: Coincident(g19,g15)
    c: Coincident(g19,g-5)
    c: Angle(g16,g19) = 1.5708
    c: Equal(g18,g19)
    c: Distance(g18) = 0.5
    c: Symmetric(g10,g11,g0)
    c: Symmetric(g9,g12,g0)
    c: Symmetric(g14,g15,g0)
    c: Horizontal(g13)
    c: PointOnObject(g17,g-4)
    c: Parallel(g10,g-3)
    c: Distance(g11) = 3
    c: Coincident(g20,g10)
    c: Angle(g-3,g20) = 1.5708
    c: PointOnObject(g20,g-3)
    c: Equal(g20,g18)
    c: Symmetric(g13,g9,g0)
FEATURE [PartDesign::Body] Body  label="TopView"
  Group = -> [Sketch003,Sketch005,Sketch006,Sketch007,Sketch008,Sketch010,Sketch011,Sketch013]
  Origin = -> Origin
